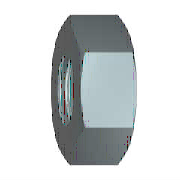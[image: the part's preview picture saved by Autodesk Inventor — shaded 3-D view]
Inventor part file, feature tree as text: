
AUTODESK INVENTOR PART (.ipt)
format: ipt  version: 2018 (Build 220112000, 112)  size: 174,080 bytes
history: native  units: mm (DEFAULTED — no unit token found)
features: sketch x3, chamfer x1, hole x1, other x1, plane x1
ambient origin geometry x7: Origin, YZ Plane, XZ Plane, X Axis, Y Axis, Z Axis, Center Point
bodies: Solid1 (feature_tree), Body (feature_tree)
feature tree (7):
  chamfer  "Chamfer1"  Angle=30.0deg  [1 undecoded]
  hole  "Thread"  [1 undecoded]
  other  "Work Axis1"
  plane  "Work Plane1"
  sketch  "Sketch1"  dims[d0=9.237604mm]
  sketch  "Sketch2"  dims[d1=5.1mm]
  sketch  "Sketch3"  dims[d2=0.0mm d3=30.0deg d4=30.0deg d5=8.0mm d6=8.0mm d7=90.0deg d25=4.134mm d26=6.0mm d27=4.0mm d28=2.0mm d29=14.3117mm d30=8.0mm d31=20.594885mm d8=0.433013mm d9=30.0deg d10=0.433013mm d11=30.0deg d13=0.0mm d14=0.0mm d39=0.0mm d40=0.433013mm d41=0.433013mm d42=0.0mm]
note: 2 required parameter values undecoded (feature->parameter linkage not recoverable at this tier; creation-order binding heuristic only, values carry confidence <= 0.55)
